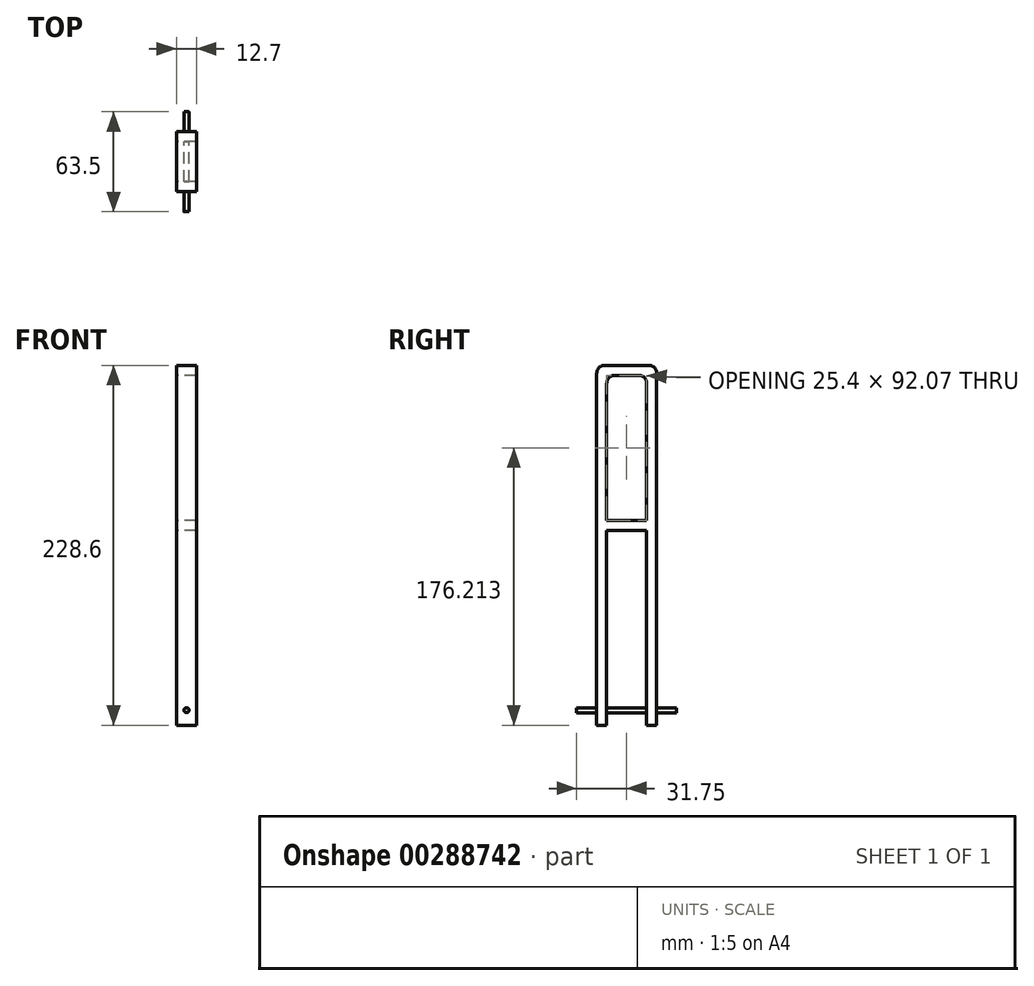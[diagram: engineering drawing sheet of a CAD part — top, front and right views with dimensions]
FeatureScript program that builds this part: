
annotation { "Feature Type Name" : "Feature", "Feature Type Description" : "" }
export const myFeature = defineFeature(function(context is Context, id is Id, definition is map)
    precondition{}
    {
        {
            var Q0;
            Q0=qCreatedBy(makeId("Right.planeOp"),FACE);
            var sketch = newSketch(context, id + "F0", { "sketchPlane" : qUnion([Q0])});
            skLineSegment(sketch, "E0", {"start": v(-12.7, 0) * mm, "end": v(-12.7, 222.25) * mm});
            skLineSegment(sketch, "E1", {"start": v(-12.7, 228.6) * mm, "end": v(-19.05, 228.6) * mm});
            skLineSegment(sketch, "E2", {"start": v(-19.05, 228.6) * mm, "end": v(-19.05, 0) * mm});
            skLineSegment(sketch, "E3", {"start": v(-19.05, 0) * mm, "end": v(-12.7, 0) * mm});
            skLineSegment(sketch, "E4.MirrorCS", {"start": v(12.7, 228.6) * mm, "end": v(19.05, 228.6) * mm});
            skLineSegment(sketch, "E5.MirrorCS", {"start": v(19.05, 0) * mm, "end": v(12.7, 0) * mm});
            skLineSegment(sketch, "E6.MirrorCS", {"start": v(12.7, 0) * mm, "end": v(12.7, 222.25) * mm});
            skLineSegment(sketch, "E7.MirrorCS", {"start": v(19.05, 228.6) * mm, "end": v(19.05, 0) * mm});
            skLineSegment(sketch, "E8", {"start": v(-12.7, 228.6) * mm, "end": v(12.7, 228.6) * mm});
            skLineSegment(sketch, "E9", {"start": v(-12.7, 222.25) * mm, "end": v(12.7, 222.25) * mm});
            skSolve(sketch);
        }
        {
            var Q0;
            Q0 = qSketchRegion(id + "F0", true);
            extrude(context, id + "F1", {"entities" : qUnion([Q0]), "endBound" : BoundingType.SYMMETRIC, "depth" : 12.7 * mm});
        }
        {
            var Q0;
            Q0=makeQuery(id+"F1.opExtrude","SWEPT_EDGE",EDGE,{"disambiguationData":[OSD([sQuery(id+"F0.wireOp",EDGE,"E0"),sQuery(id+"F0.wireOp",EDGE,"E9")])]});
            var Q1;
            Q1=makeQuery(id+"F1.opExtrude","SWEPT_EDGE",EDGE,{"disambiguationData":[OSD([sQuery(id+"F0.wireOp",EDGE,"E6.MirrorCS"),sQuery(id+"F0.wireOp",EDGE,"E9")])]});
            var Q2;
            Q2=makeQuery(id+"F1.opExtrude","SWEPT_EDGE",EDGE,{"disambiguationData":[OSD([sQuery(id+"F0.wireOp",EDGE,"E1"),sQuery(id+"F0.wireOp",EDGE,"E2")])]});
            var Q3;
            Q3=makeQuery(id+"F1.opExtrude","SWEPT_EDGE",EDGE,{"disambiguationData":[OSD([sQuery(id+"F0.wireOp",EDGE,"E4.MirrorCS"),sQuery(id+"F0.wireOp",EDGE,"E7.MirrorCS")])]});
            fillet(context, id + "F2", {"entities" : qUnion([Q0, Q1, Q2, Q3]), "radius" : 5.08 * mm, "tangentPropagation" : true, "allowEdgeOverflow" : false});
        }
        {
            var Q0;
            Q0=qCreatedBy(makeId("Front.planeOp"),FACE);
            var sketch = newSketch(context, id + "F3", { "sketchPlane" : qUnion([Q0])});
            skCircle(sketch, "E10", {"center": v(0, 9.53) * mm, "radius": 1.59 * mm});
            skLineSegment(sketch, "E11.bottom", {"start": v(6.35, 130.18) * mm, "end": v(-6.35, 130.18) * mm});
            skLineSegment(sketch, "E11.top", {"start": v(6.35, 123.83) * mm, "end": v(-6.35, 123.83) * mm});
            skLineSegment(sketch, "E11.left", {"start": v(6.35, 130.18) * mm, "end": v(6.35, 123.83) * mm});
            skLineSegment(sketch, "E11.right", {"start": v(-6.35, 130.18) * mm, "end": v(-6.35, 123.83) * mm});
            skPoint(sketch, "E11.middle", {"position": v(0, 127) * mm});
            skSolve(sketch);
        }
        {
            var Q0;
            Q0=makeQuery(id+"F3.imprint","IMPRINT",FACE,{"disambiguationData":[TD([[makeQuery(id+"F3.imprint","IMPRINT",EDGE,{"derivedFrom":sQuery(id+"F3.wireOp",EDGE,"E11.bottom")}),1.0]])]});
            extrude(context, id + "F4", {"entities" : qUnion([Q0]), "operationType" : NewBodyOperationType.ADD, "endBound" : BoundingType.SYMMETRIC, "depth" : 25.4 * mm});
        }
        {
            var Q0;
            Q0=makeQuery(id+"F3.imprint","IMPRINT",FACE,{"disambiguationData":[TD([[makeQuery(id+"F3.imprint","IMPRINT",EDGE,{"derivedFrom":sQuery(id+"F3.wireOp",EDGE,"E10")}),1.0]])]});
            extrude(context, id + "F5", {"entities" : qUnion([Q0]), "operationType" : NewBodyOperationType.REMOVE, "endBound" : BoundingType.SYMMETRIC, "oppositeDirection" : true, "depth" : 254 * mm});
        }
        {
            var Q0;
            Q0=makeQuery(id+"F3.imprint","IMPRINT",FACE,{"disambiguationData":[TD([[makeQuery(id+"F3.imprint","IMPRINT",EDGE,{"derivedFrom":sQuery(id+"F3.wireOp",EDGE,"E10")}),1.0]])]});
            var Q1;
            Q1=sQuery(id+"F3.wireOp",EDGE,"E10");
            extrude(context, id + "F6", {"entities" : qUnion([Q0]), "operationType" : NewBodyOperationType.ADD, "surfaceEntities" : qUnion([Q1]), "endBound" : BoundingType.SYMMETRIC, "depth" : 63.5 * mm});
        }
    });
